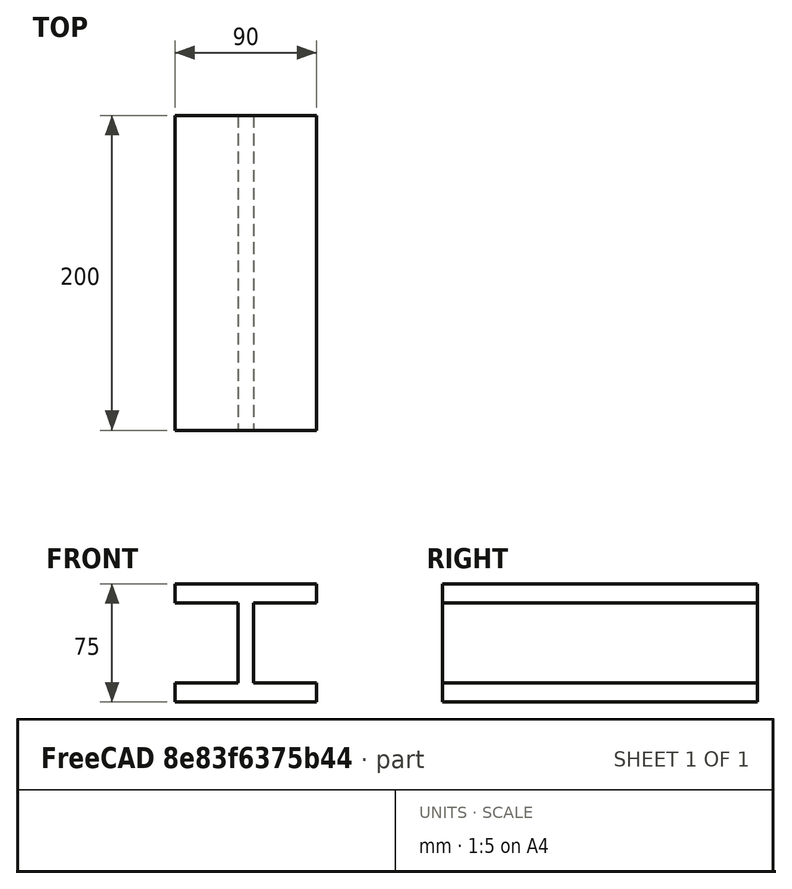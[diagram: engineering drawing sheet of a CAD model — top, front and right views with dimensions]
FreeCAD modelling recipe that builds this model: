
FCSTD DOCUMENT  (FreeCAD 0.21R33694 (Git))
Label: OJT1_T18R01_peça
License: All rights reserved
LicenseURL: http://en.wikipedia.org/wiki/All_rights_reserved
objects: Sketcher::SketchObject×1, PartDesign::Pad×1, PartDesign::Body×1
note: 4 computed .brp shape members not serialized (recipe doc carries the construction recipe); baked Part::Feature solids carry a one-line shape summary decoded from their .brp

FEATURE [Sketcher::SketchObject] Sketch
  FullyConstrained = true
  MapMode = 5
  Placement = pos=(0,0,0) rot=(1,0,0;1.5708rad)
  Support = -> [XZ_Plane]
  sketch-geometry (12):
    g0: LineSegment StartX=-38.4159 StartY=63 StartZ=0 EndX=-38.4159 EndY=51 EndZ=0
    g1: LineSegment StartX=-38.4159 StartY=51 StartZ=0 EndX=1.58409 EndY=51 EndZ=0
    g2: LineSegment StartX=1.58409 StartY=51 StartZ=0 EndX=1.58409 EndY=0 EndZ=0
    g3: LineSegment StartX=1.58409 StartY=0 StartZ=0 EndX=-38.4159 EndY=0 EndZ=0
    g4: LineSegment StartX=-38.4159 StartY=0 StartZ=0 EndX=-38.4159 EndY=-12 EndZ=0
    g5: LineSegment StartX=-38.4159 StartY=-12 StartZ=0 EndX=51.5841 EndY=-12 EndZ=0
    g6: LineSegment StartX=51.5841 StartY=-12 StartZ=0 EndX=51.5841 EndY=0 EndZ=0
    g7: LineSegment StartX=51.5841 StartY=0 StartZ=0 EndX=11.5841 EndY=0 EndZ=0
    g8: LineSegment StartX=11.5841 StartY=0 StartZ=0 EndX=11.5841 EndY=51 EndZ=0
    g9: LineSegment StartX=11.5841 StartY=51 StartZ=0 EndX=51.5841 EndY=51 EndZ=0
    g10: LineSegment StartX=51.5841 StartY=51 StartZ=0 EndX=51.5841 EndY=63 EndZ=0
    g11: LineSegment StartX=51.5841 StartY=63 StartZ=0 EndX=-38.4159 EndY=63 EndZ=0
  constraints (36):
    c: Vertical(g0)
    c: Coincident(g0,g1)
    c: Horizontal(g1)
    c: Coincident(g1,g2)
    c: Vertical(g2)
    c: Coincident(g2,g3)
    c: PointOnObject(g3,g-1)
    c: Horizontal(g3)
    c: Coincident(g3,g4)
    c: Vertical(g4)
    c: Coincident(g4,g5)
    c: Horizontal(g5)
    c: Coincident(g5,g6)
    c: Vertical(g6)
    c: Coincident(g6,g7)
    c: Horizontal(g7)
    c: Coincident(g7,g8)
    c: Vertical(g8)
    c: Coincident(g8,g9)
    c: Horizontal(g9)
    c: Coincident(g9,g10)
    c: Coincident(g10,g11)
    c: Coincident(g11,g0)
    c: Horizontal(g11)
    c: DistanceY(g2,g2) = 51
    c: Equal(g8,g2)
    c: DistanceY(g6,g6) = 12
    c: Equal(g6,g4)
    c: Equal(g4,g10)
    c: Equal(g10,g0)
    c: DistanceX(g11,g11) = 90
    c: Equal(g11,g5)
    c: DistanceX(g3,g3) = 40
    c: Equal(g1,g3)
    c: Equal(g3,g7)
    c: Equal(g7,g9)
FEATURE [PartDesign::Pad] Pad
  Direction = (0,-1,2e-16)
  Length = 200
  Length2 = 10
  Placement = pos=(0,0,0) rot=(1,0,0;1.5708rad)
  Profile = -> Sketch
  ReferenceAxis = -> Sketch [N_Axis]
  Type = 0
FEATURE [PartDesign::Body] Body
  Group = -> [Sketch,Pad]
  Origin = -> Origin
  Tip = -> Pad
